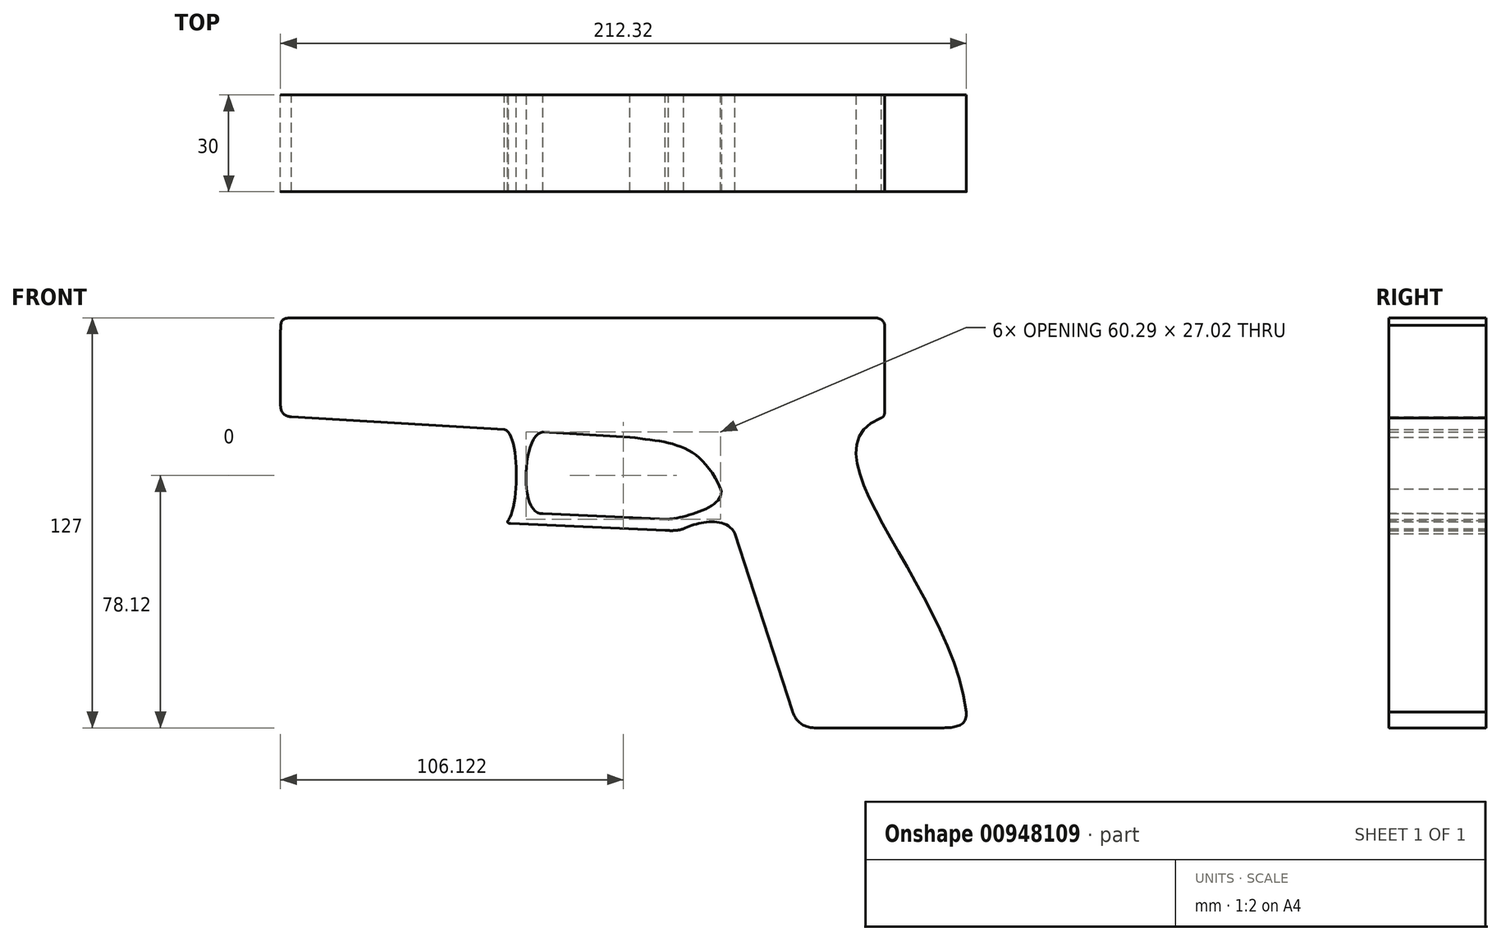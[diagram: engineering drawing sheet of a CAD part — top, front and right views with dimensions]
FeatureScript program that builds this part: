
annotation { "Feature Type Name" : "Feature", "Feature Type Description" : "" }
export const myFeature = defineFeature(function(context is Context, id is Id, definition is map)
    precondition{}
    {
        {
            var Q0;
            Q0=qCreatedBy(makeId("Front.planeOp"),FACE);
            var sketch = newSketch(context, id + "F0", { "sketchPlane" : qUnion([Q0])});
            skLineSegment(sketch, "E0.bottom", {"start": v(-80.38, 40.65) * mm, "end": v(97.78, 40.65) * mm});
            skLineSegment(sketch, "E0.top", {"start": v(-82.72, 10) * mm, "end": v(100.42, 10) * mm});
            skLineSegment(sketch, "E0.left", {"start": v(-86.1, 35.4) * mm, "end": v(-86.1, 13.74) * mm});
            skLineSegment(sketch, "E0.right", {"start": v(100.9, 38.3) * mm, "end": v(100.9, 11.84) * mm});
            skLineSegment(sketch, "E1", {"start": v(117.4, -86.35) * mm, "end": v(79.63, -86.35) * mm});
            skLineSegment(sketch, "E2", {"start": v(72.31, -81.12) * mm, "end": v(54.6, -26.15) * mm});
            skFitSpline(sketch, "E3", {"points": [v(100.9, 10) * mm, v(126.6, -86.35) * mm], "startDerivative": vector(-88.6, -29.97) * mm, "endDerivative": vector(4.32, -123.47) * mm});
            skFitSpline(sketch, "E4", {"points": [v(126.2, -81.44) * mm, v(117.4, -86.35) * mm], "startDerivative": vector(1.23, -14.74) * mm, "endDerivative": vector(-13.81, 0) * mm});
            skFitSpline(sketch, "E5", {"points": [v(72.31, -81.12) * mm, v(79.63, -86.35) * mm], "startDerivative": vector(3.68, -11.43) * mm, "endDerivative": vector(10.38, 0) * mm});
            skFitSpline(sketch, "E6", {"points": [v(-86.1, 13.74) * mm, v(-82.72, 10) * mm], "startDerivative": vector(0, -7.62) * mm, "endDerivative": vector(6.17, 0) * mm});
            skLineSegment(sketch, "E7", {"start": v(-82.72, 10) * mm, "end": v(22.05, 3.65) * mm});
            skFitSpline(sketch, "E8", {"points": [v(22.05, 3.65) * mm, v(50.17, -12.4) * mm], "startDerivative": vector(37.85, -4.88) * mm, "endDerivative": vector(19.25, -43.52) * mm});
            skFitSpline(sketch, "E9", {"points": [v(-16.8, 6) * mm, v(-16.6, -22.94) * mm], "startDerivative": vector(15.8, -3.63) * mm, "endDerivative": vector(-13.06, -4.42) * mm});
            skLineSegment(sketch, "E10", {"start": v(-14.97, -23.01) * mm, "end": v(33.02, -25.19) * mm});
            skFitSpline(sketch, "E11", {"points": [v(37.4, -25.39) * mm, v(54.6, -26.15) * mm], "startDerivative": vector(9.13, 5.67) * mm, "endDerivative": vector(10.7, -19.52) * mm});
            skLineSegment(sketch, "E12", {"start": v(-16.24, -22.75) * mm, "end": v(-16.24, -22.75) * mm});
            skLineSegment(sketch, "E13", {"start": v(-16.03, -22.6) * mm, "end": v(-16.03, -22.6) * mm});
            skFitSpline(sketch, "E14", {"points": [v(-15.49, -21.93) * mm, v(-14.97, -23.01) * mm], "startDerivative": vector(-1.64, -1.99) * mm, "endDerivative": vector(3.01, -0.14) * mm});
            skLineSegment(sketch, "E15", {"start": v(-4.82, -19.98) * mm, "end": v(34.03, -21.74) * mm});
            skFitSpline(sketch, "E16", {"points": [v(-4.82, 5.28) * mm, v(-4.82, -19.98) * mm], "startDerivative": vector(-20.13, -1.46) * mm, "endDerivative": vector(22.3, 4.47) * mm});
            skFitSpline(sketch, "E17", {"points": [v(34.03, -21.74) * mm, v(50.17, -12.4) * mm], "startDerivative": vector(9.74, 0.85) * mm, "endDerivative": vector(-5.74, 17.8) * mm});
            skFitSpline(sketch, "E18", {"points": [v(33.02, -25.19) * mm, v(38.68, -24.7) * mm], "startDerivative": vector(7.21, -0.47) * mm, "endDerivative": vector(5.6, 1.7) * mm});
            skFitSpline(sketch, "E19", {"points": [v(97.78, 40.65) * mm, v(100.9, 37.82) * mm], "startDerivative": vector(3.02, 0) * mm, "endDerivative": vector(-0.52, -7.22) * mm});
            skPoint(sketch, "E20.endDerivative.orphan", {"position": v(100.9, 40.22) * mm});
            skFitSpline(sketch, "E21", {"points": [v(-80.38, 40.65) * mm, v(-86.1, 35.4) * mm], "startDerivative": vector(-17.16, 0) * mm, "endDerivative": vector(0, -15.71) * mm});
            skFitSpline(sketch, "E22", {"points": [v(99.53, 9.48) * mm, v(100.9, 11.84) * mm], "startDerivative": vector(4.1, 1.54) * mm, "endDerivative": vector(0, 3.45) * mm});
            skLineSegment(sketch, "E23.left", {"start": v(-86.1, 23.1) * mm, "end": v(-86.1, 35.99) * mm});
            skLineSegment(sketch, "E24", {"start": v(54.6, -26.15) * mm, "end": v(42.95, 10) * mm});
            skSolve(sketch);
        }
        {
            var Q0;
            {var subQ2=sQuery(id+"F0.wireOp",EDGE,"E0.bottom");Q0=makeQuery(id+"F0.imprint","IMPRINT",FACE,{"disambiguationData":[TD([[makeQuery(id+"F0.imprint","IMPRINT",EDGE,{"derivedFrom":subQ2}),-1.0]])]});}
            var Q1;
            {var subQ6=sQuery(id+"F0.wireOp",EDGE,"E8");Q1=makeQuery(id+"F0.imprint","IMPRINT",FACE,{"disambiguationData":[TD([[makeQuery(id+"F0.imprint","IMPRINT",EDGE,{"derivedFrom":subQ6}),1.0]])]});}
            var Q2;
            Q2=makeQuery(id+"F0.imprint","IMPRINT",FACE,{"disambiguationData":[TD([[makeQuery(id+"F0.imprint","IMPRINT",EDGE,{"derivedFrom":sQuery(id+"F0.wireOp",EDGE,"E1")}),-1.0]])]});
            var Q3;
            {var subQ4=sQuery(id+"F0.wireOp",EDGE,"E10");Q3=makeQuery(id+"F0.imprint","IMPRINT",FACE,{"disambiguationData":[TD([[makeQuery(id+"F0.imprint","IMPRINT",EDGE,{"derivedFrom":subQ4}),1.0]])]});}
            extrude(context, id + "F1", {"entities" : qUnion([Q0, Q1, Q2, Q3]), "depth" : 30 * mm, "offsetDistance" : 25 * mm});
        }
    });
